# Revit family: 22M 48 Fixed
name_source: partatom
category: Furniture
revit_build: Autodesk Revit 2016 (Build: 20150220_1215(x64)
units: mm (PartAtom-declared; Revit-internal decimal feet)

## family parameters
Always vertical = Yes
Cut with Voids When Loaded = No
OmniClass Number = 23.40.20.00
OmniClass Title = General Furniture and Specialties
Room Calculation Point = No
Shared = No
Work Plane-Based = No

## types (8) — shared parameters

## per-type parameters (varying)
| type | Height | Shape |
| 22M132748EL | 2' - 3" | 22M 48 Elongated |
| 22M132748HX | 2' - 3" | 22M 48 Hex |
| 22M132748SQ | 2' - 3" | 22M 48 Square |
| 22M132748RD | 2' - 3" | 22M 48 Round |
| 22M132948SQ | 2' - 5" | 22M 48 Square |
| 22M132948EL | 2' - 5" | 22M 48 Elongated |
| 22M132948HX | 2' - 5" | 22M 48 Hex |
| 22M132948RD | 2' - 5" | 22M 48 Round |

note: column(s) folded — value = type name in every type: Model

## geometry (parser evidence)
native form markers: Sweep x12
no freeform markers — native parametric forms only
